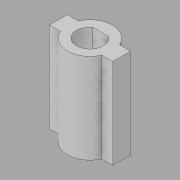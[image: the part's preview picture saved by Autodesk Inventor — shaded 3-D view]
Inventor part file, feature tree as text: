
AUTODESK INVENTOR PART (.ipt)
format: ipt  version: 2017 (Build 210142000, 142)  size: 101,888 bytes
history: native  units: mm
features: extrude x3, sketch x3
ambient origin geometry x8: Origin, YZ Plane, XZ Plane, XY Plane, X Axis, Y Axis, Z Axis, Center Point
bodies: Solid1 (feature_tree)
feature tree (6):
  extrude  "Extrusion1"  Depth=20.0mm
  extrude  "Extrusion2"  Depth=4.0mm
  extrude  "Extrusion3"  Depth=9.0mm TaperAngle=0.0deg
  sketch  "Sketch1"  dims[d0=20.0mm d1=0.0mm d2=6.0mm]
  sketch  "Sketch2"  dims[d3=9.0mm d4=0.0mm d5=4.0mm]
  sketch  "Sketch3"  dims[d6=4.0mm d7=9.0mm d8=0.0mm]
